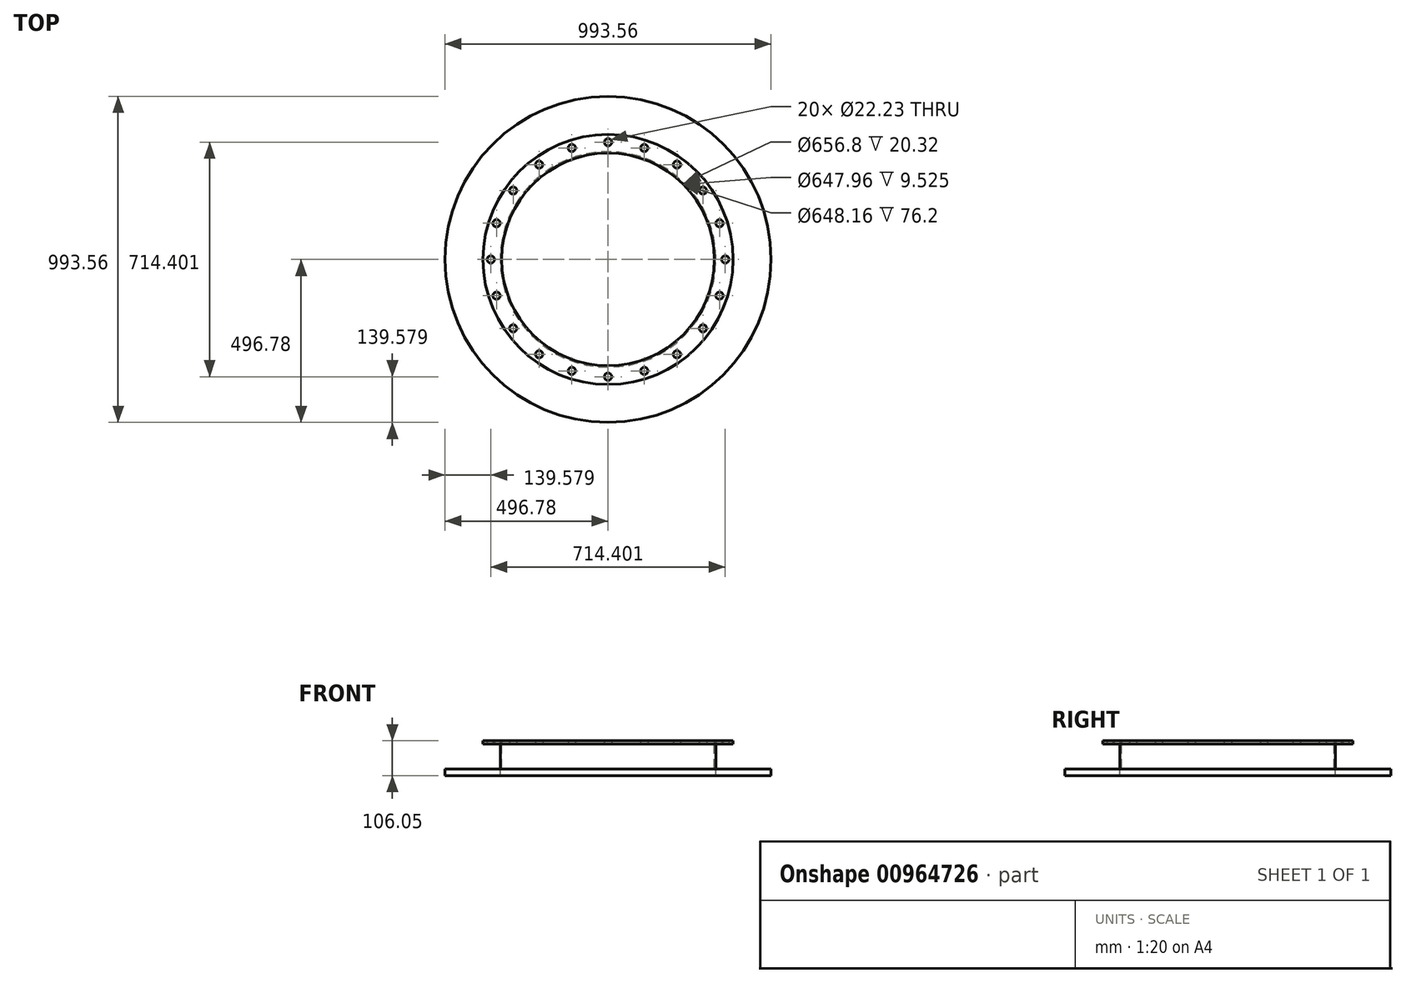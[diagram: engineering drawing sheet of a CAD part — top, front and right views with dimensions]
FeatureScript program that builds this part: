
annotation { "Feature Type Name" : "Feature", "Feature Type Description" : "" }
export const myFeature = defineFeature(function(context is Context, id is Id, definition is map)
    precondition{}
    {
        {
            var Q0;
            Q0=qCreatedBy(makeId("Top.planeOp"),FACE);
            var sketch = newSketch(context, id + "F0", { "sketchPlane" : qUnion([Q0])});
            skCircle(sketch, "E0", {"center": v(0, 0) * mm, "radius": 380.83 * mm});
            skCircle(sketch, "E1", {"center": v(0, 0) * mm, "radius": 323.98 * mm});
            skSolve(sketch);
        }
        {
            var Q0;
            Q0=makeQuery(id+"F0.imprint","IMPRINT",FACE,{"disambiguationData":[TD([[makeQuery(id+"F0.imprint","IMPRINT",EDGE,{"derivedFrom":sQuery(id+"F0.wireOp",EDGE,"E0")}),1.0]])]});
            extrude(context, id + "F1", {"entities" : qUnion([Q0]), "depth" : 9.52 * mm, "offsetDistance" : 25.4 * mm});
        }
        {
            var Q0;
            Q0=makeQuery(id+"F1.opExtrude","CAP_FACE",FACE,{"disambiguationData":[OSD([sQuery(id+"F0.wireOp",EDGE,"E0"),sQuery(id+"F0.wireOp",EDGE,"E1")])],"isStart":false});
            var sketch = newSketch(context, id + "F2", { "sketchPlane" : qUnion([Q0])});
            skCircle(sketch, "E2", {"center": v(-357.2, 0) * mm, "radius": 11.32 * mm});
            skCircle(sketch, "E3.1.0", {"center": v(-339.72, -110.38) * mm, "radius": 11.32 * mm});
            skCircle(sketch, "E3.2.0", {"center": v(-288.98, -209.96) * mm, "radius": 11.32 * mm});
            skCircle(sketch, "E3.3.0", {"center": v(-209.96, -288.98) * mm, "radius": 11.32 * mm});
            skCircle(sketch, "E3.4.0", {"center": v(-110.38, -339.72) * mm, "radius": 11.32 * mm});
            skCircle(sketch, "E3.5.0", {"center": v(0, -357.2) * mm, "radius": 11.32 * mm});
            skCircle(sketch, "E3.6.0", {"center": v(110.38, -339.72) * mm, "radius": 11.32 * mm});
            skCircle(sketch, "E3.7.0", {"center": v(209.96, -288.98) * mm, "radius": 11.32 * mm});
            skCircle(sketch, "E3.8.0", {"center": v(288.98, -209.96) * mm, "radius": 11.32 * mm});
            skCircle(sketch, "E3.9.0", {"center": v(339.72, -110.38) * mm, "radius": 11.32 * mm});
            skCircle(sketch, "E3.10.0", {"center": v(357.2, 0) * mm, "radius": 11.32 * mm});
            skCircle(sketch, "E3.11.0", {"center": v(339.72, 110.38) * mm, "radius": 11.32 * mm});
            skCircle(sketch, "E3.12.0", {"center": v(288.98, 209.96) * mm, "radius": 11.32 * mm});
            skCircle(sketch, "E3.13.0", {"center": v(209.96, 288.98) * mm, "radius": 11.32 * mm});
            skCircle(sketch, "E3.14.0", {"center": v(110.38, 339.72) * mm, "radius": 11.32 * mm});
            skCircle(sketch, "E3.15.0", {"center": v(0, 357.2) * mm, "radius": 11.32 * mm});
            skCircle(sketch, "E3.16.0", {"center": v(-110.38, 339.72) * mm, "radius": 11.32 * mm});
            skCircle(sketch, "E3.17.0", {"center": v(-209.96, 288.98) * mm, "radius": 11.32 * mm});
            skCircle(sketch, "E3.18.0", {"center": v(-288.98, 209.96) * mm, "radius": 11.32 * mm});
            skCircle(sketch, "E3.19.0", {"center": v(-339.72, 110.38) * mm, "radius": 11.32 * mm});
            skPoint(sketch, "E3.center", {"position": v(0, 0) * mm});
            skSolve(sketch);
        }
        {
            var Q0;
            Q0=sQuery(id+"F2.wireOp",VERTEX,"E3.18.0.center");
            var Q1;
            Q1=sQuery(id+"F2.wireOp",VERTEX,"E3.19.0.center");
            var Q2;
            Q2=sQuery(id+"F2.wireOp",VERTEX,"E2.center");
            var Q3;
            Q3=sQuery(id+"F2.wireOp",VERTEX,"E3.1.0.center");
            var Q4;
            Q4=sQuery(id+"F2.wireOp",VERTEX,"E3.2.0.center");
            var Q5;
            Q5=sQuery(id+"F2.wireOp",VERTEX,"E3.3.0.center");
            var Q6;
            Q6=sQuery(id+"F2.wireOp",VERTEX,"E3.4.0.center");
            var Q7;
            Q7=sQuery(id+"F2.wireOp",VERTEX,"E3.5.0.center");
            var Q8;
            Q8=sQuery(id+"F2.wireOp",VERTEX,"E3.6.0.center");
            var Q9;
            Q9=sQuery(id+"F2.wireOp",VERTEX,"E3.7.0.center");
            var Q10;
            Q10=sQuery(id+"F2.wireOp",VERTEX,"E3.8.0.center");
            var Q11;
            Q11=sQuery(id+"F2.wireOp",VERTEX,"E3.9.0.center");
            var Q12;
            Q12=sQuery(id+"F2.wireOp",VERTEX,"E3.10.0.center");
            var Q13;
            Q13=sQuery(id+"F2.wireOp",VERTEX,"E3.11.0.center");
            var Q14;
            Q14=sQuery(id+"F2.wireOp",VERTEX,"E3.12.0.center");
            var Q15;
            Q15=sQuery(id+"F2.wireOp",VERTEX,"E3.13.0.center");
            var Q16;
            Q16=sQuery(id+"F2.wireOp",VERTEX,"E3.14.0.center");
            var Q17;
            Q17=sQuery(id+"F2.wireOp",VERTEX,"E3.15.0.center");
            var Q18;
            Q18=sQuery(id+"F2.wireOp",VERTEX,"E3.16.0.center");
            var Q19;
            Q19=sQuery(id+"F2.wireOp",VERTEX,"E3.17.0.center");
            var Q20;
            Q20=makeQuery(id+"F1.opExtrude","SWEPT_BODY",BODY,{"disambiguationData":[OSD([sQuery(id+"F0.wireOp",EDGE,"E0"),sQuery(id+"F0.wireOp",EDGE,"E1")])]});
            hole(context, id + "F3", {"style" : HoleStyle.SIMPLE, "endStyle" : HoleEndStyle.THROUGH, "holeDiameter" : 22.22 * mm, "majorDiameter" : 6.35 * mm, "isTappedThrough" : true, "tappedDepth" : 12.7 * mm, "tapClearance" : 3, "locations" : qUnion([Q0, Q1, Q2, Q3, Q4, Q5, Q6, Q7, Q8, Q9, Q10, Q11, Q12, Q13, Q14, Q15, Q16, Q17, Q18, Q19]), "scope" : qUnion([Q20]), "startStyle" : HoleStartStyle.SKETCH});
        }
        {
            var Q0;
            Q0=makeQuery(id+"F0.imprint","IMPRINT",FACE,{"disambiguationData":[TD([[makeQuery(id+"F0.imprint","IMPRINT",EDGE,{"derivedFrom":sQuery(id+"F0.wireOp",EDGE,"E0")}),1.0]])]});
            var sketch = newSketch(context, id + "F4", { "sketchPlane" : qUnion([Q0])});
            skCircle(sketch, "E4", {"center": v(0, 0) * mm, "radius": 328.4 * mm});
            skCircle(sketch, "E5", {"center": v(0, 0) * mm, "radius": 324.08 * mm});
            skSolve(sketch);
        }
        {
            var Q0;
            Q0=qSketchRegion(id+"F4",true);
            extrude(context, id + "F5", {"entities" : qUnion([Q0]), "operationType" : NewBodyOperationType.ADD, "oppositeDirection" : true, "depth" : 76.2 * mm, "offsetDistance" : 25.4 * mm});
        }
        {
            var Q0;
            Q0=makeQuery(id+"F5.opExtrude","CAP_FACE",FACE,{"disambiguationData":[OSD([sQuery(id+"F4.wireOp",EDGE,"E4"),sQuery(id+"F4.wireOp",EDGE,"E5")])],"isStart":false});
            var sketch = newSketch(context, id + "F6", { "sketchPlane" : qUnion([Q0])});
            skCircle(sketch, "E6", {"center": v(0, 0) * mm, "radius": 496.78 * mm});
            skSolve(sketch);
        }
        {
            var Q0;
            Q0=makeQuery(id+"F6.imprint","IMPRINT",FACE,{"disambiguationData":[TD([[makeQuery(id+"F6.imprint","IMPRINT",EDGE,{"derivedFrom":sQuery(id+"F6.wireOp",EDGE,"E6")}),1.0]])]});
            extrude(context, id + "F7", {"entities" : qUnion([Q0]), "depth" : 20.32 * mm, "offsetDistance" : 25.4 * mm});
        }
    });
